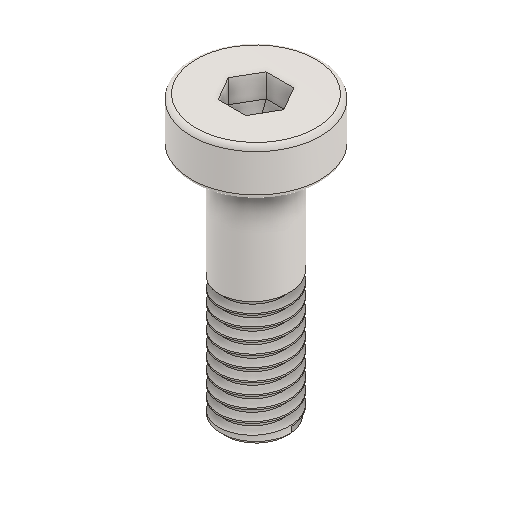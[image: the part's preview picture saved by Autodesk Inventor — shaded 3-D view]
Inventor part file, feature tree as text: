
AUTODESK INVENTOR PART (.ipt)
format: ipt  version: 2022 (Build 260153000, 153)  size: 295,936 bytes
history: mixed  units: in
note: dims shown in document units (in); Inventor stores cm internally (conversion verified against a paired STEP export)
features: fillet x1, imported_body x1
ambient origin geometry x8: Origin, YZ Plane, XZ Plane, XY Plane, X Axis, Y Axis, Z Axis, Center Point
bodies: Solid1 (imported_parasolid)
feature tree (2):
  fillet  "Fillet1"  [1 undecoded]
  imported_body  NMx_Import_Brep_tag  [imported B-rep: ~6 faces, bbox_mm=None]
note: 1 required parameter value undecoded (feature->parameter linkage not recoverable at this tier; creation-order binding heuristic only, values carry confidence <= 0.55)
